# Revit family: STH21952BR_27_STH21952PTO_27
name_source: partatom
category: Luminárias
units: mm (PartAtom-declared; Revit-internal decimal feet)

## family parameters
Compartilhado = Não
Corte com vazios quando carregada = Não
Cota do conector redondo = Utilizar diâmetro
Fonte luminosa = Não
Hospedeiro = Forro
Manter orientação da anotação = Não
Número OmniClass = 23.80.70.11
Ponto de cálculo do ambiente = Não
Sempre na vertical = Sim
Tipo de parte = Normal
Título OmniClass = Luminaries for Internal Lighting

## types (2) — shared parameters
Altura = 0.01 m
Comprimento = 2.02 m
Dimerização = Não dimerizável
Fabricante = Stella
Grau de proteção (IP) = IP20
IRC (Índice de reprodução de cores) = >93 (R9 >60)
Largura = 0.02 m
Luminoso = Luminoso - 2700K
Modelo = Archi
Potência = 10 W
Referência = STH21952BR/27 - BRANCO - 2m
Temperatura da cor (K) = 2700 K
Tensão Elétrica = 24V
URL = https://stella.com.br
Ângulo de Abertura = 110°
zero-valued in all types: Elevação padrão

## per-type parameters (varying)
| type | Estrutura | Fluxo Luminoso | Fluxo Luminoso STH21952BR/27 | Fluxo Luminoso STH21952PTO/27 |
| STH21952BR/27 - BRANCO - 2m - 2700K - 440lm - 110° | Al - Branco | 440 lm | Sim | Não |
| STH21952PTO/27 - PRETO - 2m - 2700K - 220lm - 110° | Al - Preto | 220 lm | Não | Sim |
